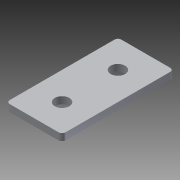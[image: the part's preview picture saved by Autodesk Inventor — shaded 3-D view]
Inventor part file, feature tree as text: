
AUTODESK INVENTOR PART (.ipt)
format: ipt  version: 2013 (Build 170138000, 138)  size: 90,112 bytes
history: native  units: in
note: dims shown in document units (in); Inventor stores cm internally (conversion verified against a paired STEP export)
features: extrude x1, fillet x1, sketch x1
ambient origin geometry x8: Origin, YZ Plane, XZ Plane, XY Plane, X Axis, Y Axis, Z Axis, Center Point
bodies: Solid1 (feature_tree)
feature tree (3):
  extrude  "Extrusion1"  Depth=1.0in
  fillet  "Fillet1"  Radius=0.26in
  sketch  "Sketch1"  dims[d0=2.0in d1=1.0in d2=0.26in d3=0.26in d4=1.0in d5=0.125in d6=0.0in d7=0.0625in]
